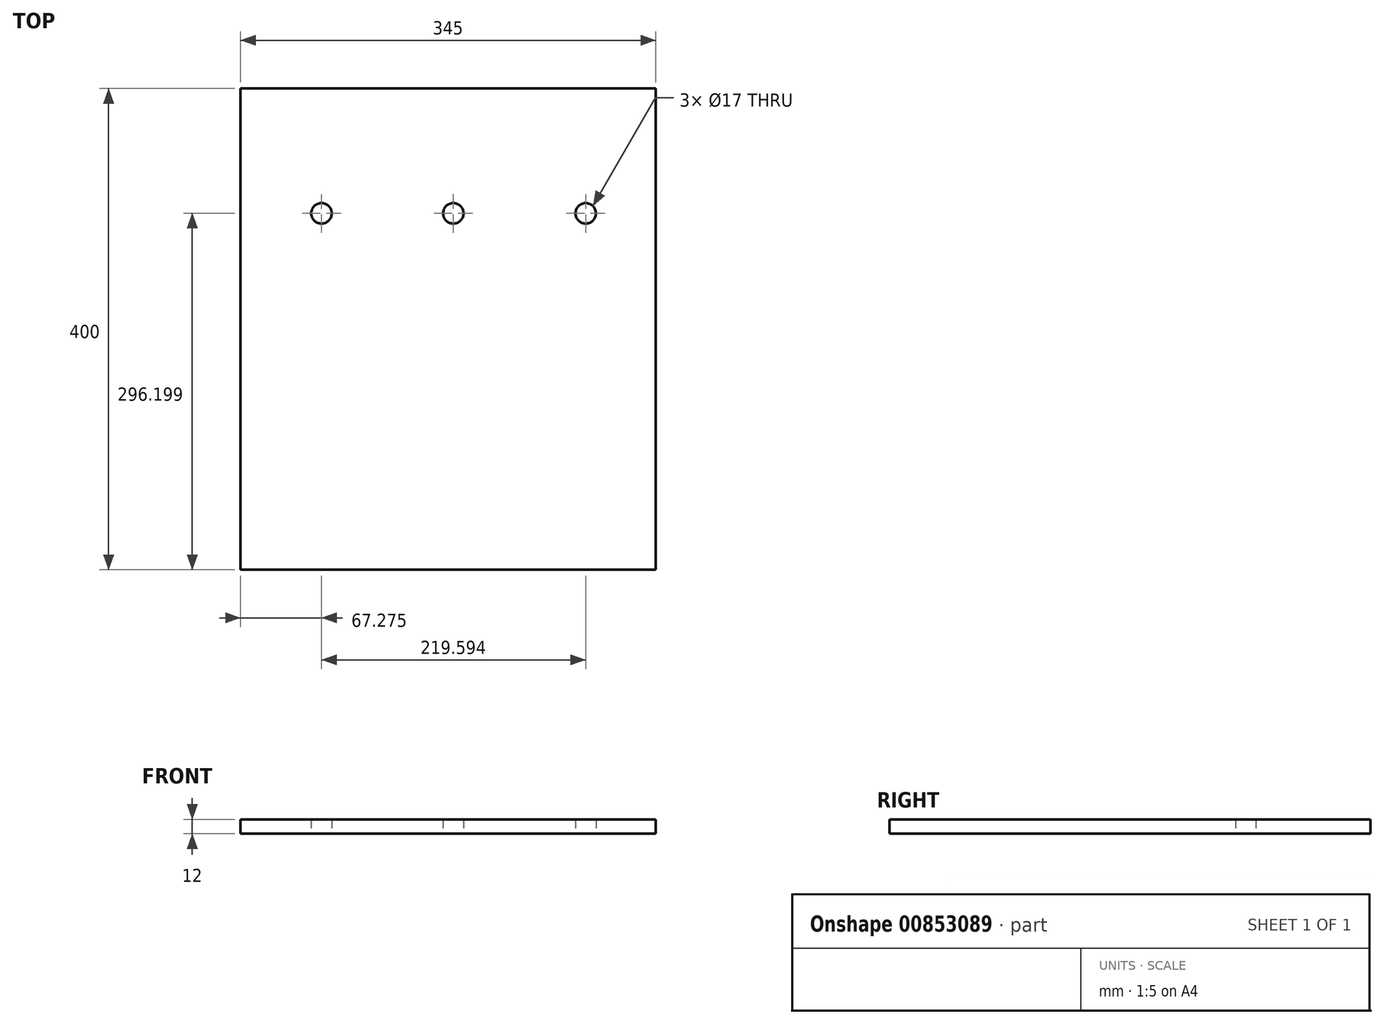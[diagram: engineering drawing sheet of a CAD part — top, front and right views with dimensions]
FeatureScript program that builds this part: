
annotation { "Feature Type Name" : "Feature", "Feature Type Description" : "" }
export const myFeature = defineFeature(function(context is Context, id is Id, definition is map)
    precondition{}
    {
        {
            var Q0;
            Q0=qCreatedBy(makeId("Top.planeOp"),FACE);
            var sketch = newSketch(context, id + "F0", { "sketchPlane" : qUnion([Q0])});
            skLineSegment(sketch, "E0.bottom", {"start": v(-235.43, 154.94) * mm, "end": v(109.57, 154.94) * mm});
            skLineSegment(sketch, "E0.top", {"start": v(-235.43, -245.06) * mm, "end": v(109.57, -245.06) * mm});
            skLineSegment(sketch, "E0.left", {"start": v(-235.43, 154.94) * mm, "end": v(-235.43, -245.06) * mm});
            skLineSegment(sketch, "E0.right", {"start": v(109.57, 154.94) * mm, "end": v(109.57, -245.06) * mm});
            skPoint(sketch, "E1", {"position": v(-168.15, 51.14) * mm});
            skPoint(sketch, "E2", {"position": v(-58.61, 51.14) * mm});
            skPoint(sketch, "E3", {"position": v(51.44, 51.14) * mm});
            skSolve(sketch);
        }
        {
            var Q0;
            Q0 = qSketchRegion(id + "F0", true);
            extrude(context, id + "F1", {"entities" : qUnion([Q0]), "depth" : 12 * mm, "offsetDistance" : 25 * mm});
        }
        {
            var Q0;
            Q0=sQuery(id+"F0.wireOp",VERTEX,"E1");
            var Q1;
            Q1=sQuery(id+"F0.wireOp",VERTEX,"E2");
            var Q2;
            Q2=sQuery(id+"F0.wireOp",VERTEX,"E3");
            var Q3;
            Q3=makeQuery(id+"F1.opExtrude","SWEPT_BODY",BODY,{"disambiguationData":[OSD([sQuery(id+"F0.wireOp",EDGE,"E0.bottom"),sQuery(id+"F0.wireOp",EDGE,"E0.top"),sQuery(id+"F0.wireOp",EDGE,"E0.left"),sQuery(id+"F0.wireOp",EDGE,"E0.right")])]});
            hole(context, id + "F2", {"style" : HoleStyle.SIMPLE, "endStyle" : HoleEndStyle.BLIND, "oppositeDirection" : true, "holeDiameter" : 17 * mm, "majorDiameter" : 4.17 * mm, "holeDepth" : 12 * mm, "isTappedThrough" : true, "tappedDepth" : 6.4 * mm, "tapClearance" : 3, "startFromSketch" : true, "locations" : qUnion([Q0, Q1, Q2]), "scope" : qUnion([Q3])});
        }
    });
